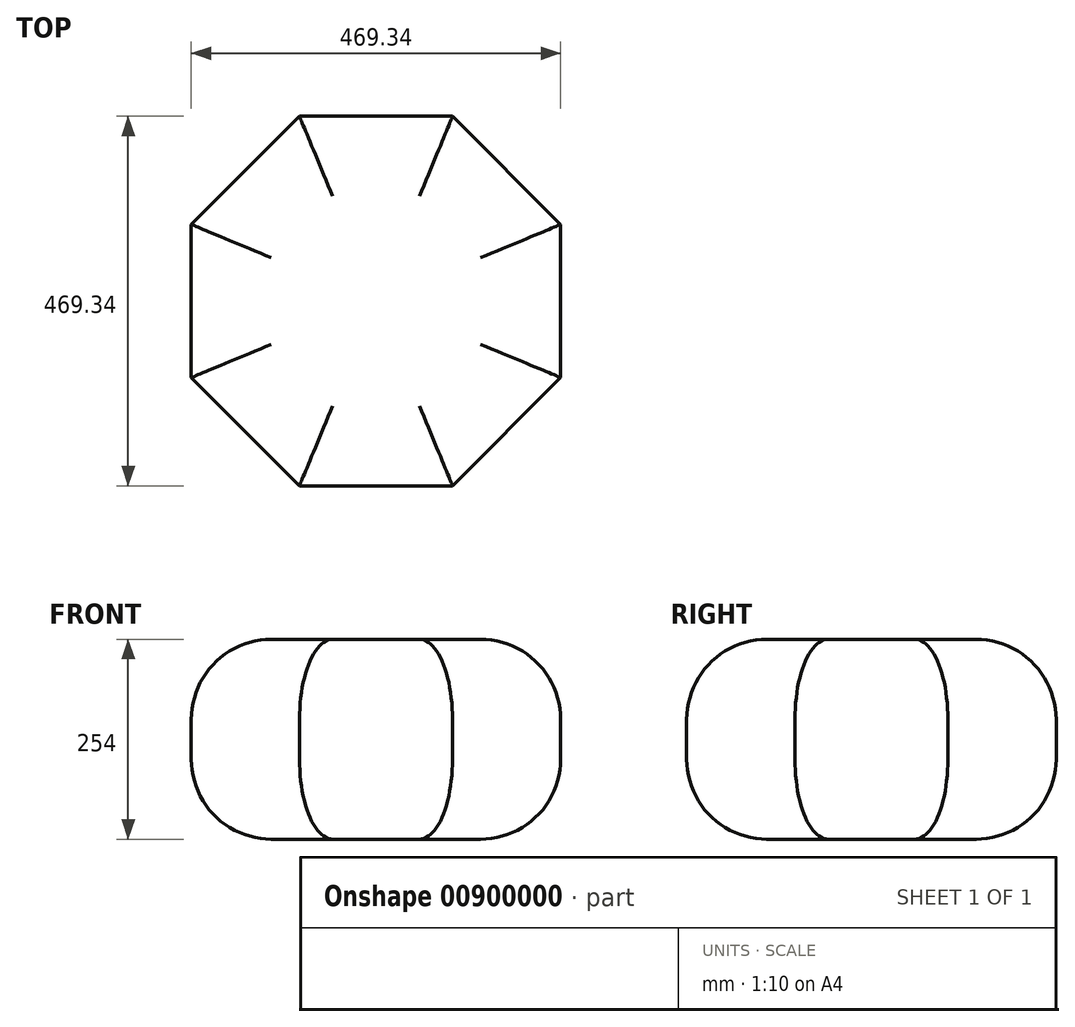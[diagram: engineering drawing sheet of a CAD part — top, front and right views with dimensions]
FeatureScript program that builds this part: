
annotation { "Feature Type Name" : "Feature", "Feature Type Description" : "" }
export const myFeature = defineFeature(function(context is Context, id is Id, definition is map)
    precondition{}
    {
        {
            var Q0;
            Q0=qCreatedBy(makeId("Top.planeOp"),FACE);
            var sketch = newSketch(context, id + "F0", { "sketchPlane" : qUnion([Q0])});
            skCircle(sketch, "E0.cCircle", {"center": v(0, 0) * mm, "radius": 234.67 * mm, "construction": true});
            skLineSegment(sketch, "E0.0", {"start": v(-97.2, 234.67) * mm, "end": v(97.2, 234.67) * mm});
            skLineSegment(sketch, "E0.1", {"start": v(97.2, 234.67) * mm, "end": v(234.67, 97.2) * mm});
            skLineSegment(sketch, "E0.2", {"start": v(234.67, 97.2) * mm, "end": v(234.67, -97.2) * mm});
            skLineSegment(sketch, "E0.3", {"start": v(234.67, -97.2) * mm, "end": v(97.2, -234.67) * mm});
            skLineSegment(sketch, "E0.4", {"start": v(97.2, -234.67) * mm, "end": v(-97.2, -234.67) * mm});
            skLineSegment(sketch, "E0.5", {"start": v(-97.2, -234.67) * mm, "end": v(-234.67, -97.2) * mm});
            skLineSegment(sketch, "E0.6", {"start": v(-234.67, -97.2) * mm, "end": v(-234.67, 97.2) * mm});
            skLineSegment(sketch, "E0.7", {"start": v(-234.67, 97.2) * mm, "end": v(-97.2, 234.67) * mm});
            skPoint(sketch, "E0.0.midPoint", {"position": v(0, 234.67) * mm});
            skSolve(sketch);
        }
        {
            var Q0;
            Q0=makeQuery(id+"F0.imprint","IMPRINT",FACE,{"disambiguationData":[TD([[makeQuery(id+"F0.imprint","IMPRINT",EDGE,{"derivedFrom":sQuery(id+"F0.wireOp",EDGE,"E0.0")}),-1.0]])]});
            extrude(context, id + "F1", {"entities" : qUnion([Q0]), "depth" : 254 * mm, "offsetDistance" : 25.4 * mm});
        }
        {
            var Q0;
            Q0=makeQuery(id+"F1.opExtrude","CAP_FACE",FACE,{"disambiguationData":[OSD([sQuery(id+"F0.wireOp",EDGE,"E0.0"),sQuery(id+"F0.wireOp",EDGE,"E0.1"),sQuery(id+"F0.wireOp",EDGE,"E0.2"),sQuery(id+"F0.wireOp",EDGE,"E0.3"),sQuery(id+"F0.wireOp",EDGE,"E0.4"),sQuery(id+"F0.wireOp",EDGE,"E0.5"),sQuery(id+"F0.wireOp",EDGE,"E0.6"),sQuery(id+"F0.wireOp",EDGE,"E0.7")])],"isStart":true});
            var Q1;
            Q1=makeQuery(id+"F1.opExtrude","CAP_FACE",FACE,{"disambiguationData":[OSD([sQuery(id+"F0.wireOp",EDGE,"E0.0"),sQuery(id+"F0.wireOp",EDGE,"E0.1"),sQuery(id+"F0.wireOp",EDGE,"E0.2"),sQuery(id+"F0.wireOp",EDGE,"E0.3"),sQuery(id+"F0.wireOp",EDGE,"E0.4"),sQuery(id+"F0.wireOp",EDGE,"E0.5"),sQuery(id+"F0.wireOp",EDGE,"E0.6"),sQuery(id+"F0.wireOp",EDGE,"E0.7")])],"isStart":false});
            fillet(context, id + "F2", {"entities" : qUnion([Q0, Q1]), "radius" : 101.6 * mm, "tangentPropagation" : true, "allowEdgeOverflow" : false});
        }
    });
